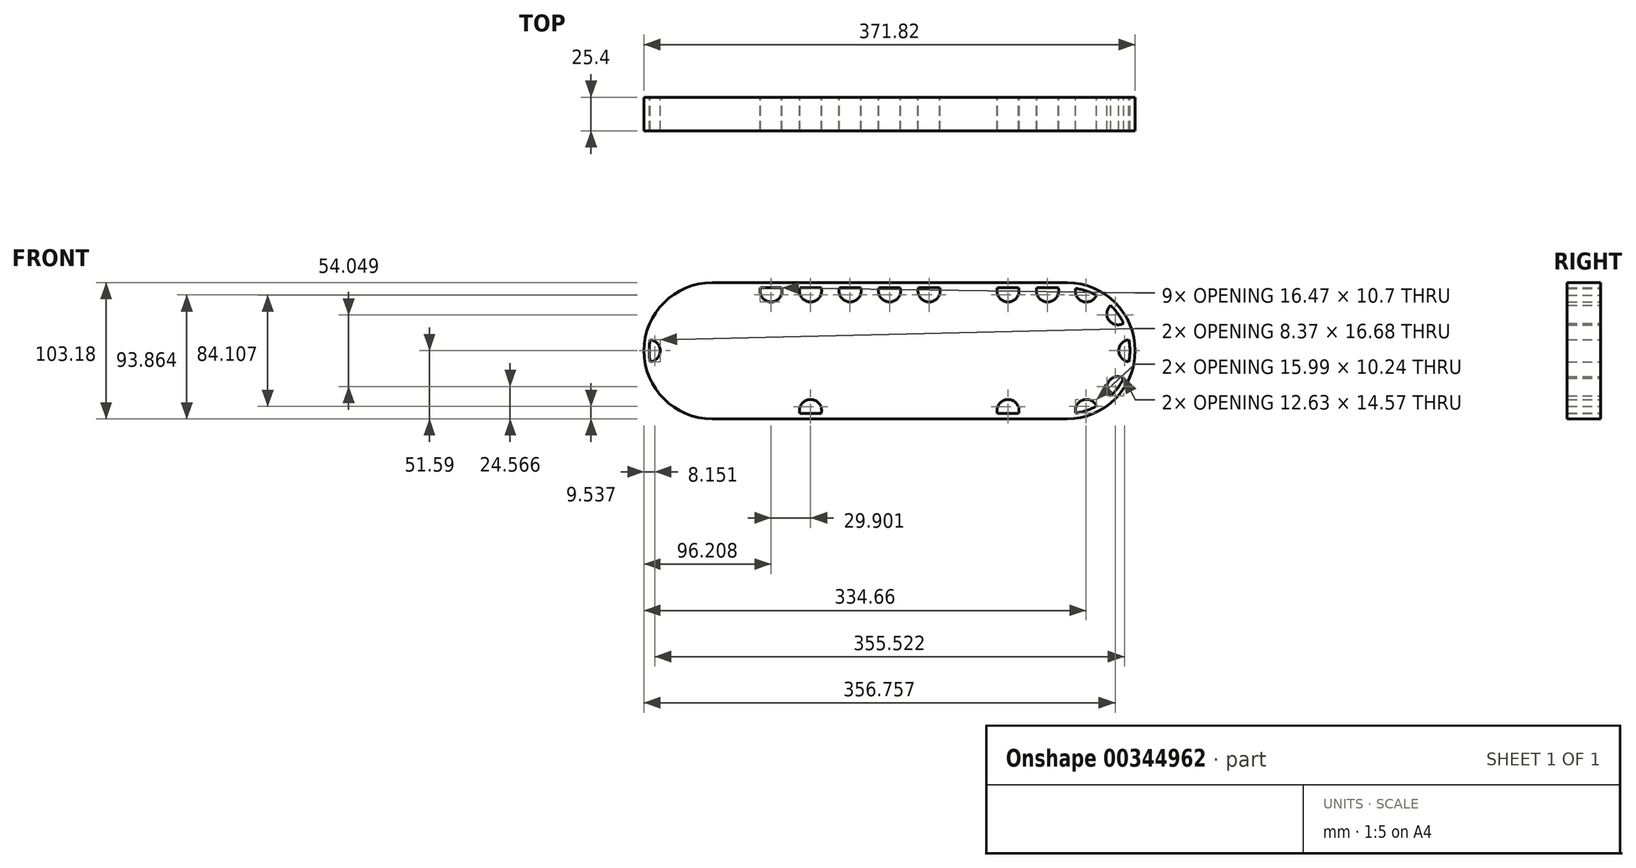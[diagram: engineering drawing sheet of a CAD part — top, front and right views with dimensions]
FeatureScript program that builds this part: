
annotation { "Feature Type Name" : "Feature", "Feature Type Description" : "" }
export const myFeature = defineFeature(function(context is Context, id is Id, definition is map)
    precondition{}
    {
        {
            var Q0;
            Q0=qCreatedBy(makeId("Front.planeOp"),FACE);
            var sketch = newSketch(context, id + "F0", { "sketchPlane" : qUnion([Q0])});
            skCircle(sketch, "E0", {"center": v(0, 0) * mm, "radius": 9.53 * mm});
            skCircle(sketch, "E1", {"center": v(0, 0) * mm, "radius": 15.88 * mm});
            skCircle(sketch, "E2", {"center": v(0, 0) * mm, "radius": 25.4 * mm});
            skCircle(sketch, "E3", {"center": v(0, 0) * mm, "radius": 38.1 * mm});
            skArc(sketch, "E4", {"start": v(5.87, 47.26) * mm, "mid": v(0, 47.63) * mm, "end": v(-5.87, 47.26) * mm});
            skLineSegment(sketch, "E5", {"start": v(-5.87, 47.26) * mm, "end": v(-7.62, 37.33) * mm});
            skLineSegment(sketch, "E6", {"start": v(5.87, 47.26) * mm, "end": v(7.62, 37.33) * mm});
            skLineSegment(sketch, "E7.1.0", {"start": v(-32.53, 34.79) * mm, "end": v(-28.1, 25.72) * mm});
            skArc(sketch, "E7.1.1", {"start": v(-23.03, 41.69) * mm, "mid": v(-28, 38.53) * mm, "end": v(-32.53, 34.79) * mm});
            skLineSegment(sketch, "E7.1.2", {"start": v(-23.03, 41.69) * mm, "end": v(-15.78, 34.68) * mm});
            skLineSegment(sketch, "E7.2.0", {"start": v(-46.76, 9.02) * mm, "end": v(-37.86, 4.29) * mm});
            skArc(sketch, "E7.2.1", {"start": v(-43.14, 20.19) * mm, "mid": v(-45.3, 14.72) * mm, "end": v(-46.76, 9.02) * mm});
            skLineSegment(sketch, "E7.2.2", {"start": v(-43.14, 20.19) * mm, "end": v(-33.15, 18.78) * mm});
            skLineSegment(sketch, "E7.3.0", {"start": v(-43.14, -20.19) * mm, "end": v(-33.15, -18.78) * mm});
            skArc(sketch, "E7.3.1", {"start": v(-46.76, -9.02) * mm, "mid": v(-45.3, -14.72) * mm, "end": v(-43.14, -20.19) * mm});
            skLineSegment(sketch, "E7.3.2", {"start": v(-46.76, -9.02) * mm, "end": v(-37.86, -4.29) * mm});
            skLineSegment(sketch, "E7.4.0", {"start": v(-23.03, -41.69) * mm, "end": v(-15.78, -34.68) * mm});
            skArc(sketch, "E7.4.1", {"start": v(-32.53, -34.79) * mm, "mid": v(-28, -38.53) * mm, "end": v(-23.03, -41.69) * mm});
            skLineSegment(sketch, "E7.4.2", {"start": v(-32.53, -34.79) * mm, "end": v(-28.1, -25.72) * mm});
            skLineSegment(sketch, "E7.5.0", {"start": v(5.87, -47.26) * mm, "end": v(7.62, -37.33) * mm});
            skArc(sketch, "E7.5.1", {"start": v(-5.87, -47.26) * mm, "mid": v(0, -47.63) * mm, "end": v(5.87, -47.26) * mm});
            skLineSegment(sketch, "E7.5.2", {"start": v(-5.87, -47.26) * mm, "end": v(-7.62, -37.33) * mm});
            skLineSegment(sketch, "E7.6.0", {"start": v(32.53, -34.79) * mm, "end": v(28.1, -25.72) * mm});
            skArc(sketch, "E7.6.1", {"start": v(23.03, -41.69) * mm, "mid": v(28, -38.53) * mm, "end": v(32.53, -34.79) * mm});
            skLineSegment(sketch, "E7.6.2", {"start": v(23.03, -41.69) * mm, "end": v(15.78, -34.68) * mm});
            skLineSegment(sketch, "E7.7.0", {"start": v(46.76, -9.02) * mm, "end": v(37.86, -4.29) * mm});
            skArc(sketch, "E7.7.1", {"start": v(43.14, -20.19) * mm, "mid": v(45.3, -14.72) * mm, "end": v(46.76, -9.02) * mm});
            skLineSegment(sketch, "E7.7.2", {"start": v(43.14, -20.19) * mm, "end": v(33.15, -18.78) * mm});
            skLineSegment(sketch, "E7.8.0", {"start": v(43.14, 20.19) * mm, "end": v(33.15, 18.78) * mm});
            skArc(sketch, "E7.8.1", {"start": v(46.76, 9.02) * mm, "mid": v(45.3, 14.72) * mm, "end": v(43.14, 20.19) * mm});
            skLineSegment(sketch, "E7.8.2", {"start": v(46.76, 9.02) * mm, "end": v(37.86, 4.29) * mm});
            skLineSegment(sketch, "E7.9.0", {"start": v(23.03, 41.69) * mm, "end": v(15.78, 34.68) * mm});
            skArc(sketch, "E7.9.1", {"start": v(32.53, 34.79) * mm, "mid": v(28, 38.53) * mm, "end": v(23.03, 41.69) * mm});
            skLineSegment(sketch, "E7.9.2", {"start": v(32.53, 34.79) * mm, "end": v(28.1, 25.72) * mm});
            skLineSegment(sketch, "E8", {"start": v(-3.98, 25.09) * mm, "end": v(-3.98, 15.37) * mm, "construction": true});
            skLineSegment(sketch, "E9", {"start": v(3.98, 25.09) * mm, "end": v(3.98, 15.37) * mm, "construction": true});
            skLineSegment(sketch, "E10.1.0", {"start": v(-19.74, -15.99) * mm, "end": v(-11.32, -11.13) * mm, "construction": true});
            skLineSegment(sketch, "E10.1.1", {"start": v(-23.71, -9.1) * mm, "end": v(-15.3, -4.24) * mm, "construction": true});
            skLineSegment(sketch, "E10.2.0", {"start": v(23.71, -9.1) * mm, "end": v(15.3, -4.24) * mm, "construction": true});
            skLineSegment(sketch, "E10.2.1", {"start": v(19.74, -15.99) * mm, "end": v(11.32, -11.13) * mm, "construction": true});
            skSolve(sketch);
        }
        {
            var Q0;
            Q0=qCreatedBy(makeId("Front.planeOp"),FACE);
            var sketch = newSketch(context, id + "F1", { "sketchPlane" : qUnion([Q0])});
            skArc(sketch, "E11", {"start": v(23.03, 41.69) * mm, "mid": v(-10.34, 46.49) * mm, "end": v(-38.53, 28) * mm});
            skLineSegment(sketch, "E12.0", {"start": v(23.03, 41.69) * mm, "end": v(15.78, 34.68) * mm, "construction": true});
            skLineSegment(sketch, "E12.1", {"start": v(5.87, 47.26) * mm, "end": v(7.62, 37.33) * mm, "construction": true});
            skLineSegment(sketch, "E12.2", {"start": v(-5.87, 47.26) * mm, "end": v(-7.62, 37.33) * mm, "construction": true});
            skLineSegment(sketch, "E12.3", {"start": v(-23.03, 41.69) * mm, "end": v(-15.78, 34.68) * mm, "construction": true});
            skLineSegment(sketch, "E12.4", {"start": v(-32.53, 34.79) * mm, "end": v(-28.1, 25.72) * mm, "construction": true});
            skLineSegment(sketch, "E12.5", {"start": v(-43.14, 20.19) * mm, "end": v(-33.15, 18.78) * mm, "construction": true});
            skLineSegment(sketch, "E12.6", {"start": v(-46.76, 9.02) * mm, "end": v(-37.86, 4.29) * mm, "construction": true});
            skLineSegment(sketch, "E12.7", {"start": v(-46.76, -9.02) * mm, "end": v(-37.86, -4.29) * mm, "construction": true});
            skCircle(sketch, "E13", {"center": v(-14.72, 45.3) * mm, "radius": 8.37 * mm});
            skCircle(sketch, "E14", {"center": v(-38.53, 28) * mm, "radius": 8.37 * mm});
            skCircle(sketch, "E15", {"center": v(-47.62, 0) * mm, "radius": 8.37 * mm});
            skCircle(sketch, "E16", {"center": v(14.72, 45.3) * mm, "radius": 8.37 * mm});
            skLineSegment(sketch, "E17", {"start": v(-14.72, 45.3) * mm, "end": v(14.72, 45.3) * mm, "construction": true});
            skArc(sketch, "E18.trimOffspring", {"start": v(-42.84, 20.81) * mm, "mid": v(-45.3, 14.72) * mm, "end": v(-46.89, 8.34) * mm});
            skArc(sketch, "E19.trimOffspring", {"start": v(-47.62, 0) * mm, "mid": v(-24.2, -41.02) * mm, "end": v(23.03, -41.69) * mm});
            skLineSegment(sketch, "E20", {"start": v(14.72, 45.3) * mm, "end": v(44.62, 45.3) * mm, "construction": true});
            skLineSegment(sketch, "E21", {"start": v(44.62, 45.3) * mm, "end": v(74.52, 45.3) * mm, "construction": true});
            skLineSegment(sketch, "E22", {"start": v(74.52, 45.3) * mm, "end": v(104.42, 45.3) * mm, "construction": true});
            skLineSegment(sketch, "E23", {"start": v(104.42, 45.3) * mm, "end": v(134.32, 45.3) * mm, "construction": true});
            skCircle(sketch, "E24", {"center": v(44.62, 45.3) * mm, "radius": 8.37 * mm});
            skCircle(sketch, "E25", {"center": v(74.52, 45.3) * mm, "radius": 8.37 * mm});
            skCircle(sketch, "E26", {"center": v(104.42, 45.3) * mm, "radius": 8.37 * mm});
            skCircle(sketch, "E27", {"center": v(134.32, 45.3) * mm, "radius": 8.37 * mm});
            skPoint(sketch, "E28", {"position": v(23.09, 45.3) * mm});
            skPoint(sketch, "E29", {"position": v(36.25, 45.3) * mm});
            skLineSegment(sketch, "E30", {"start": v(0, 0) * mm, "end": v(134.32, 0) * mm, "construction": true});
            skLineSegment(sketch, "E31", {"start": v(134.32, 45.3) * mm, "end": v(134.32, 0) * mm, "construction": true});
            skCircle(sketch, "E32.MirrorC", {"center": v(134.32, -45.3) * mm, "radius": 8.37 * mm});
            skCircle(sketch, "E33.MirrorC", {"center": v(104.42, -45.3) * mm, "radius": 8.37 * mm});
            skCircle(sketch, "E34.MirrorC", {"center": v(74.52, -45.3) * mm, "radius": 8.37 * mm});
            skCircle(sketch, "E35.MirrorC", {"center": v(44.62, -45.3) * mm, "radius": 8.37 * mm});
            skCircle(sketch, "E36.MirrorC", {"center": v(14.72, -45.3) * mm, "radius": 8.37 * mm});
            skCircle(sketch, "E37.MirrorC", {"center": v(-14.72, -45.3) * mm, "radius": 8.37 * mm});
            skCircle(sketch, "E38.MirrorC", {"center": v(-38.53, -28) * mm, "radius": 8.37 * mm});
            skCircle(sketch, "E39.MirrorC", {"center": v(164.22, 45.3) * mm, "radius": 8.37 * mm});
            skCircle(sketch, "E40.MirrorC", {"center": v(194.12, 45.3) * mm, "radius": 8.37 * mm});
            skCircle(sketch, "E41.MirrorC", {"center": v(224.03, 45.3) * mm, "radius": 8.37 * mm});
            skCircle(sketch, "E42.MirrorC", {"center": v(253.93, 45.3) * mm, "radius": 8.37 * mm});
            skCircle(sketch, "E43.MirrorC", {"center": v(283.36, 45.3) * mm, "radius": 8.37 * mm});
            skCircle(sketch, "E44.MirrorC", {"center": v(307.17, 28) * mm, "radius": 8.37 * mm});
            skCircle(sketch, "E45.MirrorC", {"center": v(316.27, 0) * mm, "radius": 8.37 * mm});
            skCircle(sketch, "E46.MirrorC", {"center": v(307.17, -28) * mm, "radius": 8.37 * mm});
            skCircle(sketch, "E47.MirrorC", {"center": v(283.36, -45.3) * mm, "radius": 8.37 * mm});
            skCircle(sketch, "E48.MirrorC", {"center": v(253.93, -45.3) * mm, "radius": 8.37 * mm});
            skCircle(sketch, "E49.MirrorC", {"center": v(224.03, -45.3) * mm, "radius": 8.37 * mm});
            skCircle(sketch, "E50.MirrorC", {"center": v(194.12, -45.3) * mm, "radius": 8.37 * mm});
            skCircle(sketch, "E51.MirrorC", {"center": v(164.22, -45.3) * mm, "radius": 8.37 * mm});
            skSolve(sketch);
        }
        {
            var Q0;
            Q0=qCreatedBy(makeId("Front.planeOp"),FACE);
            var sketch = newSketch(context, id + "F2", { "sketchPlane" : qUnion([Q0])});
            skArc(sketch, "E52", {"start": v(0, 47.62) * mm, "mid": v(-47.62, 0) * mm, "end": v(0, -47.62) * mm});
            skLineSegment(sketch, "E53", {"start": v(0, 47.62) * mm, "end": v(268.64, 47.62) * mm});
            skLineSegment(sketch, "E54", {"start": v(0, -47.62) * mm, "end": v(268.64, -47.62) * mm});
            skLineSegment(sketch, "E55.0", {"start": v(134.32, 45.3) * mm, "end": v(134.32, 0) * mm, "construction": true});
            skLineSegment(sketch, "E56.0", {"start": v(0, 0) * mm, "end": v(134.32, 0) * mm, "construction": true});
            skLineSegment(sketch, "E57.MirrorCS", {"start": v(268.64, 0) * mm, "end": v(134.32, 0) * mm, "construction": true});
            skArc(sketch, "E58", {"start": v(268.64, 47.62) * mm, "mid": v(316.27, 0) * mm, "end": v(268.64, -47.62) * mm});
            skLineSegment(sketch, "E59.0", {"start": v(0, 51.59) * mm, "end": v(268.64, 51.59) * mm});
            skArc(sketch, "E59.1", {"start": v(0, 51.59) * mm, "mid": v(-51.59, 0) * mm, "end": v(0, -51.59) * mm});
            skLineSegment(sketch, "E59.2", {"start": v(0, -51.59) * mm, "end": v(268.64, -51.59) * mm});
            skArc(sketch, "E59.3", {"start": v(268.64, 51.59) * mm, "mid": v(320.23, 0) * mm, "end": v(268.64, -51.59) * mm});
            skArc(sketch, "E60.0", {"start": v(98.9, 51.59) * mm, "mid": v(104.42, 36.92) * mm, "end": v(109.94, 51.59) * mm});
            skArc(sketch, "E60.1", {"start": v(69, 51.59) * mm, "mid": v(74.52, 36.92) * mm, "end": v(80.04, 51.59) * mm});
            skArc(sketch, "E60.2", {"start": v(39.1, 51.59) * mm, "mid": v(44.62, 36.92) * mm, "end": v(50.14, 51.59) * mm});
            skArc(sketch, "E60.3", {"start": v(9.2, 51.59) * mm, "mid": v(14.72, 36.92) * mm, "end": v(20.24, 51.59) * mm});
            skArc(sketch, "E60.4", {"start": v(-23.04, 46.15) * mm, "mid": v(-12.13, 37.33) * mm, "end": v(-8.49, 50.88) * mm});
            skArc(sketch, "E60.5", {"start": v(-45.77, 23.8) * mm, "mid": v(-31.76, 23.07) * mm, "end": v(-36.77, 36.18) * mm});
            skArc(sketch, "E60.6", {"start": v(-51.02, -7.65) * mm, "mid": v(-39.25, 0) * mm, "end": v(-51.02, 7.65) * mm});
            skArc(sketch, "E60.7", {"start": v(-45.77, -23.8) * mm, "mid": v(-31.76, -23.07) * mm, "end": v(-36.77, -36.18) * mm});
            skArc(sketch, "E60.8", {"start": v(-23.04, -46.15) * mm, "mid": v(-12.13, -37.33) * mm, "end": v(-8.49, -50.88) * mm});
            skArc(sketch, "E60.9", {"start": v(9.2, -51.59) * mm, "mid": v(14.72, -36.92) * mm, "end": v(20.24, -51.59) * mm});
            skArc(sketch, "E60.10", {"start": v(39.1, -51.59) * mm, "mid": v(44.62, -36.92) * mm, "end": v(50.14, -51.59) * mm});
            skArc(sketch, "E60.11", {"start": v(69, -51.59) * mm, "mid": v(74.52, -36.92) * mm, "end": v(80.04, -51.59) * mm});
            skArc(sketch, "E60.12", {"start": v(98.9, -51.59) * mm, "mid": v(104.42, -36.92) * mm, "end": v(109.94, -51.59) * mm});
            skArc(sketch, "E60.13", {"start": v(128.8, -51.59) * mm, "mid": v(134.32, -36.92) * mm, "end": v(139.84, -51.59) * mm});
            skArc(sketch, "E60.14", {"start": v(169.74, -51.59) * mm, "mid": v(164.22, -36.92) * mm, "end": v(158.7, -51.59) * mm});
            skArc(sketch, "E60.15", {"start": v(199.65, -51.59) * mm, "mid": v(194.12, -36.92) * mm, "end": v(188.6, -51.59) * mm});
            skArc(sketch, "E60.16", {"start": v(229.55, -51.59) * mm, "mid": v(224.03, -36.92) * mm, "end": v(218.5, -51.59) * mm});
            skArc(sketch, "E60.17", {"start": v(259.45, -51.59) * mm, "mid": v(253.93, -36.92) * mm, "end": v(248.4, -51.59) * mm});
            skArc(sketch, "E60.18", {"start": v(291.69, -46.15) * mm, "mid": v(280.77, -37.33) * mm, "end": v(277.13, -50.88) * mm});
            skArc(sketch, "E60.19", {"start": v(314.42, -23.8) * mm, "mid": v(300.4, -23.07) * mm, "end": v(305.42, -36.18) * mm});
            skArc(sketch, "E60.20", {"start": v(319.66, -7.65) * mm, "mid": v(307.9, 0) * mm, "end": v(319.66, 7.65) * mm});
            skArc(sketch, "E60.21", {"start": v(314.42, 23.8) * mm, "mid": v(300.4, 23.07) * mm, "end": v(305.42, 36.18) * mm});
            skArc(sketch, "E60.22", {"start": v(291.69, 46.15) * mm, "mid": v(280.77, 37.33) * mm, "end": v(277.13, 50.88) * mm});
            skArc(sketch, "E60.23", {"start": v(259.45, 51.59) * mm, "mid": v(253.93, 36.92) * mm, "end": v(248.4, 51.59) * mm});
            skArc(sketch, "E60.24", {"start": v(229.55, 51.59) * mm, "mid": v(224.03, 36.92) * mm, "end": v(218.5, 51.59) * mm});
            skArc(sketch, "E60.25", {"start": v(199.65, 51.59) * mm, "mid": v(194.12, 36.92) * mm, "end": v(188.6, 51.59) * mm});
            skArc(sketch, "E60.26", {"start": v(169.74, 51.59) * mm, "mid": v(164.22, 36.92) * mm, "end": v(158.7, 51.59) * mm});
            skArc(sketch, "E60.27", {"start": v(128.8, 51.59) * mm, "mid": v(134.32, 36.92) * mm, "end": v(139.84, 51.59) * mm});
            skSolve(sketch);
        }
        {
            var Q0;
            Q0 = qSketchRegion(id + "F2", true);
            var Q1;
            {var subQ0=sQuery(id+"F2.wireOp",EDGE,"E60.6");var subQ1=sQuery(id+"F2.wireOp",EDGE,"E52");var subQ2=makeQuery(id+"F2.imprint","INTERSECT",VERTEX,{"disambiguationData":[OD(0.0)],"derivedFrom":[subQ1,subQ0]});Q1=makeQuery(id+"F2.imprint","IMPRINT",FACE,{"disambiguationData":[TD([[makeQuery(id+"F2.imprint","IMPRINT",EDGE,{"disambiguationData":[TD([[subQ2,-1.0]])],"derivedFrom":subQ1}),1.0]])]});}
            var Q2;
            {var subQ0=sQuery(id+"F2.wireOp",EDGE,"E60.7");var subQ1=sQuery(id+"F2.wireOp",EDGE,"E52");var subQ2=makeQuery(id+"F2.imprint","INTERSECT",VERTEX,{"disambiguationData":[OD(0.0)],"derivedFrom":[subQ1,subQ0]});Q2=makeQuery(id+"F2.imprint","IMPRINT",FACE,{"disambiguationData":[TD([[makeQuery(id+"F2.imprint","IMPRINT",EDGE,{"disambiguationData":[TD([[subQ2,-1.0]])],"derivedFrom":subQ1}),1.0]])]});}
            var Q3;
            {var subQ0=sQuery(id+"F2.wireOp",EDGE,"E60.8");var subQ1=sQuery(id+"F2.wireOp",EDGE,"E52");var subQ2=makeQuery(id+"F2.imprint","INTERSECT",VERTEX,{"disambiguationData":[OD(0.0)],"derivedFrom":[subQ1,subQ0]});Q3=makeQuery(id+"F2.imprint","IMPRINT",FACE,{"disambiguationData":[TD([[makeQuery(id+"F2.imprint","IMPRINT",EDGE,{"disambiguationData":[TD([[subQ2,-1.0]])],"derivedFrom":subQ1}),1.0]])]});}
            var Q4;
            {var subQ0=sQuery(id+"F2.wireOp",EDGE,"E60.9");var subQ1=sQuery(id+"F2.wireOp",EDGE,"E54");var subQ2=makeQuery(id+"F2.imprint","INTERSECT",VERTEX,{"disambiguationData":[OD(0.0)],"derivedFrom":[subQ1,subQ0]});Q4=makeQuery(id+"F2.imprint","IMPRINT",FACE,{"disambiguationData":[TD([[makeQuery(id+"F2.imprint","IMPRINT",EDGE,{"disambiguationData":[TD([[subQ2,-1.0]])],"derivedFrom":subQ1}),1.0]])]});}
            var Q5;
            {var subQ0=sQuery(id+"F2.wireOp",EDGE,"E60.10");var subQ1=sQuery(id+"F2.wireOp",EDGE,"E54");var subQ2=makeQuery(id+"F2.imprint","INTERSECT",VERTEX,{"disambiguationData":[OD(0.0)],"derivedFrom":[subQ1,subQ0]});Q5=makeQuery(id+"F2.imprint","IMPRINT",FACE,{"disambiguationData":[TD([[makeQuery(id+"F2.imprint","IMPRINT",EDGE,{"disambiguationData":[TD([[subQ2,-1.0]])],"derivedFrom":subQ1}),1.0]])]});}
            var Q6;
            {var subQ0=sQuery(id+"F2.wireOp",EDGE,"E60.11");var subQ1=sQuery(id+"F2.wireOp",EDGE,"E54");var subQ2=makeQuery(id+"F2.imprint","INTERSECT",VERTEX,{"disambiguationData":[OD(0.0)],"derivedFrom":[subQ1,subQ0]});Q6=makeQuery(id+"F2.imprint","IMPRINT",FACE,{"disambiguationData":[TD([[makeQuery(id+"F2.imprint","IMPRINT",EDGE,{"disambiguationData":[TD([[subQ2,-1.0]])],"derivedFrom":subQ1}),1.0]])]});}
            var Q7;
            {var subQ0=sQuery(id+"F2.wireOp",EDGE,"E60.12");var subQ1=sQuery(id+"F2.wireOp",EDGE,"E54");var subQ2=makeQuery(id+"F2.imprint","INTERSECT",VERTEX,{"disambiguationData":[OD(0.0)],"derivedFrom":[subQ1,subQ0]});Q7=makeQuery(id+"F2.imprint","IMPRINT",FACE,{"disambiguationData":[TD([[makeQuery(id+"F2.imprint","IMPRINT",EDGE,{"disambiguationData":[TD([[subQ2,-1.0]])],"derivedFrom":subQ1}),1.0]])]});}
            var Q8;
            {var subQ0=sQuery(id+"F2.wireOp",EDGE,"E60.13");var subQ1=sQuery(id+"F2.wireOp",EDGE,"E54");var subQ2=makeQuery(id+"F2.imprint","INTERSECT",VERTEX,{"disambiguationData":[OD(0.0)],"derivedFrom":[subQ1,subQ0]});Q8=makeQuery(id+"F2.imprint","IMPRINT",FACE,{"disambiguationData":[TD([[makeQuery(id+"F2.imprint","IMPRINT",EDGE,{"disambiguationData":[TD([[subQ2,-1.0]])],"derivedFrom":subQ1}),1.0]])]});}
            var Q9;
            {var subQ0=sQuery(id+"F2.wireOp",EDGE,"E60.14");var subQ1=sQuery(id+"F2.wireOp",EDGE,"E54");var subQ2=makeQuery(id+"F2.imprint","INTERSECT",VERTEX,{"disambiguationData":[OD(0.0)],"derivedFrom":[subQ1,subQ0]});Q9=makeQuery(id+"F2.imprint","IMPRINT",FACE,{"disambiguationData":[TD([[makeQuery(id+"F2.imprint","IMPRINT",EDGE,{"disambiguationData":[TD([[subQ2,-1.0]])],"derivedFrom":subQ1}),1.0]])]});}
            var Q10;
            {var subQ0=sQuery(id+"F2.wireOp",EDGE,"E60.15");var subQ1=sQuery(id+"F2.wireOp",EDGE,"E54");var subQ2=makeQuery(id+"F2.imprint","INTERSECT",VERTEX,{"disambiguationData":[OD(0.0)],"derivedFrom":[subQ1,subQ0]});Q10=makeQuery(id+"F2.imprint","IMPRINT",FACE,{"disambiguationData":[TD([[makeQuery(id+"F2.imprint","IMPRINT",EDGE,{"disambiguationData":[TD([[subQ2,-1.0]])],"derivedFrom":subQ1}),1.0]])]});}
            var Q11;
            {var subQ0=sQuery(id+"F2.wireOp",EDGE,"E60.16");var subQ1=sQuery(id+"F2.wireOp",EDGE,"E54");var subQ2=makeQuery(id+"F2.imprint","INTERSECT",VERTEX,{"disambiguationData":[OD(0.0)],"derivedFrom":[subQ1,subQ0]});Q11=makeQuery(id+"F2.imprint","IMPRINT",FACE,{"disambiguationData":[TD([[makeQuery(id+"F2.imprint","IMPRINT",EDGE,{"disambiguationData":[TD([[subQ2,-1.0]])],"derivedFrom":subQ1}),1.0]])]});}
            var Q12;
            {var subQ0=sQuery(id+"F2.wireOp",EDGE,"E60.17");var subQ1=sQuery(id+"F2.wireOp",EDGE,"E54");var subQ2=makeQuery(id+"F2.imprint","INTERSECT",VERTEX,{"disambiguationData":[OD(0.0)],"derivedFrom":[subQ1,subQ0]});Q12=makeQuery(id+"F2.imprint","IMPRINT",FACE,{"disambiguationData":[TD([[makeQuery(id+"F2.imprint","IMPRINT",EDGE,{"disambiguationData":[TD([[subQ2,-1.0]])],"derivedFrom":subQ1}),1.0]])]});}
            var Q13;
            {var subQ0=sQuery(id+"F2.wireOp",EDGE,"E60.18");var subQ1=sQuery(id+"F2.wireOp",EDGE,"E58");var subQ2=makeQuery(id+"F2.imprint","INTERSECT",VERTEX,{"disambiguationData":[OD(0.0)],"derivedFrom":[subQ1,subQ0]});Q13=makeQuery(id+"F2.imprint","IMPRINT",FACE,{"disambiguationData":[TD([[makeQuery(id+"F2.imprint","IMPRINT",EDGE,{"disambiguationData":[TD([[subQ2,-1.0]])],"derivedFrom":subQ1}),-1.0]])]});}
            var Q14;
            {var subQ0=sQuery(id+"F2.wireOp",EDGE,"E60.19");var subQ1=sQuery(id+"F2.wireOp",EDGE,"E58");var subQ2=makeQuery(id+"F2.imprint","INTERSECT",VERTEX,{"disambiguationData":[OD(0.0)],"derivedFrom":[subQ1,subQ0]});Q14=makeQuery(id+"F2.imprint","IMPRINT",FACE,{"disambiguationData":[TD([[makeQuery(id+"F2.imprint","IMPRINT",EDGE,{"disambiguationData":[TD([[subQ2,-1.0]])],"derivedFrom":subQ1}),-1.0]])]});}
            var Q15;
            {var subQ0=sQuery(id+"F2.wireOp",EDGE,"E60.20");var subQ1=sQuery(id+"F2.wireOp",EDGE,"E58");var subQ2=makeQuery(id+"F2.imprint","INTERSECT",VERTEX,{"disambiguationData":[OD(0.0)],"derivedFrom":[subQ1,subQ0]});Q15=makeQuery(id+"F2.imprint","IMPRINT",FACE,{"disambiguationData":[TD([[makeQuery(id+"F2.imprint","IMPRINT",EDGE,{"disambiguationData":[TD([[subQ2,-1.0]])],"derivedFrom":subQ1}),-1.0]])]});}
            var Q16;
            {var subQ0=sQuery(id+"F2.wireOp",EDGE,"E60.21");var subQ1=sQuery(id+"F2.wireOp",EDGE,"E58");var subQ2=makeQuery(id+"F2.imprint","INTERSECT",VERTEX,{"disambiguationData":[OD(0.0)],"derivedFrom":[subQ1,subQ0]});Q16=makeQuery(id+"F2.imprint","IMPRINT",FACE,{"disambiguationData":[TD([[makeQuery(id+"F2.imprint","IMPRINT",EDGE,{"disambiguationData":[TD([[subQ2,-1.0]])],"derivedFrom":subQ1}),-1.0]])]});}
            var Q17;
            {var subQ0=sQuery(id+"F2.wireOp",EDGE,"E60.22");var subQ1=sQuery(id+"F2.wireOp",EDGE,"E58");var subQ2=makeQuery(id+"F2.imprint","INTERSECT",VERTEX,{"disambiguationData":[OD(0.0)],"derivedFrom":[subQ1,subQ0]});Q17=makeQuery(id+"F2.imprint","IMPRINT",FACE,{"disambiguationData":[TD([[makeQuery(id+"F2.imprint","IMPRINT",EDGE,{"disambiguationData":[TD([[subQ2,-1.0]])],"derivedFrom":subQ1}),-1.0]])]});}
            var Q18;
            {var subQ0=sQuery(id+"F2.wireOp",EDGE,"E60.23");var subQ1=sQuery(id+"F2.wireOp",EDGE,"E53");var subQ2=makeQuery(id+"F2.imprint","INTERSECT",VERTEX,{"disambiguationData":[OD(0.0)],"derivedFrom":[subQ1,subQ0]});Q18=makeQuery(id+"F2.imprint","IMPRINT",FACE,{"disambiguationData":[TD([[makeQuery(id+"F2.imprint","IMPRINT",EDGE,{"disambiguationData":[TD([[subQ2,-1.0]])],"derivedFrom":subQ1}),-1.0]])]});}
            var Q19;
            {var subQ0=sQuery(id+"F2.wireOp",EDGE,"E60.24");var subQ1=sQuery(id+"F2.wireOp",EDGE,"E53");var subQ2=makeQuery(id+"F2.imprint","INTERSECT",VERTEX,{"disambiguationData":[OD(0.0)],"derivedFrom":[subQ1,subQ0]});Q19=makeQuery(id+"F2.imprint","IMPRINT",FACE,{"disambiguationData":[TD([[makeQuery(id+"F2.imprint","IMPRINT",EDGE,{"disambiguationData":[TD([[subQ2,-1.0]])],"derivedFrom":subQ1}),-1.0]])]});}
            var Q20;
            {var subQ0=sQuery(id+"F2.wireOp",EDGE,"E60.25");var subQ1=sQuery(id+"F2.wireOp",EDGE,"E53");var subQ2=makeQuery(id+"F2.imprint","INTERSECT",VERTEX,{"disambiguationData":[OD(0.0)],"derivedFrom":[subQ1,subQ0]});Q20=makeQuery(id+"F2.imprint","IMPRINT",FACE,{"disambiguationData":[TD([[makeQuery(id+"F2.imprint","IMPRINT",EDGE,{"disambiguationData":[TD([[subQ2,-1.0]])],"derivedFrom":subQ1}),-1.0]])]});}
            var Q21;
            {var subQ0=sQuery(id+"F2.wireOp",EDGE,"E60.26");var subQ1=sQuery(id+"F2.wireOp",EDGE,"E53");var subQ2=makeQuery(id+"F2.imprint","INTERSECT",VERTEX,{"disambiguationData":[OD(0.0)],"derivedFrom":[subQ1,subQ0]});Q21=makeQuery(id+"F2.imprint","IMPRINT",FACE,{"disambiguationData":[TD([[makeQuery(id+"F2.imprint","IMPRINT",EDGE,{"disambiguationData":[TD([[subQ2,-1.0]])],"derivedFrom":subQ1}),-1.0]])]});}
            var Q22;
            {var subQ0=sQuery(id+"F2.wireOp",EDGE,"E60.27");var subQ1=sQuery(id+"F2.wireOp",EDGE,"E53");var subQ2=makeQuery(id+"F2.imprint","INTERSECT",VERTEX,{"disambiguationData":[OD(0.0)],"derivedFrom":[subQ1,subQ0]});Q22=makeQuery(id+"F2.imprint","IMPRINT",FACE,{"disambiguationData":[TD([[makeQuery(id+"F2.imprint","IMPRINT",EDGE,{"disambiguationData":[TD([[subQ2,-1.0]])],"derivedFrom":subQ1}),-1.0]])]});}
            var Q23;
            {var subQ0=sQuery(id+"F2.wireOp",EDGE,"E60.0");var subQ1=sQuery(id+"F2.wireOp",EDGE,"E53");var subQ2=makeQuery(id+"F2.imprint","INTERSECT",VERTEX,{"disambiguationData":[OD(0.0)],"derivedFrom":[subQ1,subQ0]});Q23=makeQuery(id+"F2.imprint","IMPRINT",FACE,{"disambiguationData":[TD([[makeQuery(id+"F2.imprint","IMPRINT",EDGE,{"disambiguationData":[TD([[subQ2,-1.0]])],"derivedFrom":subQ1}),-1.0]])]});}
            var Q24;
            {var subQ0=sQuery(id+"F2.wireOp",EDGE,"E60.1");var subQ1=sQuery(id+"F2.wireOp",EDGE,"E53");var subQ2=makeQuery(id+"F2.imprint","INTERSECT",VERTEX,{"disambiguationData":[OD(0.0)],"derivedFrom":[subQ1,subQ0]});Q24=makeQuery(id+"F2.imprint","IMPRINT",FACE,{"disambiguationData":[TD([[makeQuery(id+"F2.imprint","IMPRINT",EDGE,{"disambiguationData":[TD([[subQ2,-1.0]])],"derivedFrom":subQ1}),-1.0]])]});}
            var Q25;
            {var subQ0=sQuery(id+"F2.wireOp",EDGE,"E60.2");var subQ1=sQuery(id+"F2.wireOp",EDGE,"E53");var subQ2=makeQuery(id+"F2.imprint","INTERSECT",VERTEX,{"disambiguationData":[OD(0.0)],"derivedFrom":[subQ1,subQ0]});Q25=makeQuery(id+"F2.imprint","IMPRINT",FACE,{"disambiguationData":[TD([[makeQuery(id+"F2.imprint","IMPRINT",EDGE,{"disambiguationData":[TD([[subQ2,-1.0]])],"derivedFrom":subQ1}),-1.0]])]});}
            var Q26;
            {var subQ0=sQuery(id+"F2.wireOp",EDGE,"E60.3");var subQ1=sQuery(id+"F2.wireOp",EDGE,"E53");var subQ2=makeQuery(id+"F2.imprint","INTERSECT",VERTEX,{"disambiguationData":[OD(0.0)],"derivedFrom":[subQ1,subQ0]});Q26=makeQuery(id+"F2.imprint","IMPRINT",FACE,{"disambiguationData":[TD([[makeQuery(id+"F2.imprint","IMPRINT",EDGE,{"disambiguationData":[TD([[subQ2,-1.0]])],"derivedFrom":subQ1}),-1.0]])]});}
            var Q27;
            {var subQ0=sQuery(id+"F2.wireOp",EDGE,"E60.4");var subQ1=sQuery(id+"F2.wireOp",EDGE,"E52");var subQ2=makeQuery(id+"F2.imprint","INTERSECT",VERTEX,{"disambiguationData":[OD(0.0)],"derivedFrom":[subQ1,subQ0]});Q27=makeQuery(id+"F2.imprint","IMPRINT",FACE,{"disambiguationData":[TD([[makeQuery(id+"F2.imprint","IMPRINT",EDGE,{"disambiguationData":[TD([[subQ2,-1.0]])],"derivedFrom":subQ1}),1.0]])]});}
            var Q28;
            {var subQ0=sQuery(id+"F2.wireOp",EDGE,"E60.5");var subQ1=sQuery(id+"F2.wireOp",EDGE,"E52");var subQ2=makeQuery(id+"F2.imprint","INTERSECT",VERTEX,{"disambiguationData":[OD(0.0)],"derivedFrom":[subQ1,subQ0]});Q28=makeQuery(id+"F2.imprint","IMPRINT",FACE,{"disambiguationData":[TD([[makeQuery(id+"F2.imprint","IMPRINT",EDGE,{"disambiguationData":[TD([[subQ2,-1.0]])],"derivedFrom":subQ1}),1.0]])]});}
            extrude(context, id + "F3", {"entities" : qUnion([Q0, Q1, Q2, Q3, Q4, Q5, Q6, Q7, Q8, Q9, Q10, Q11, Q12, Q13, Q14, Q15, Q16, Q17, Q18, Q19, Q20, Q21, Q22, Q23, Q24, Q25, Q26, Q27, Q28]), "depth" : 25.4 * mm});
        }
    });
